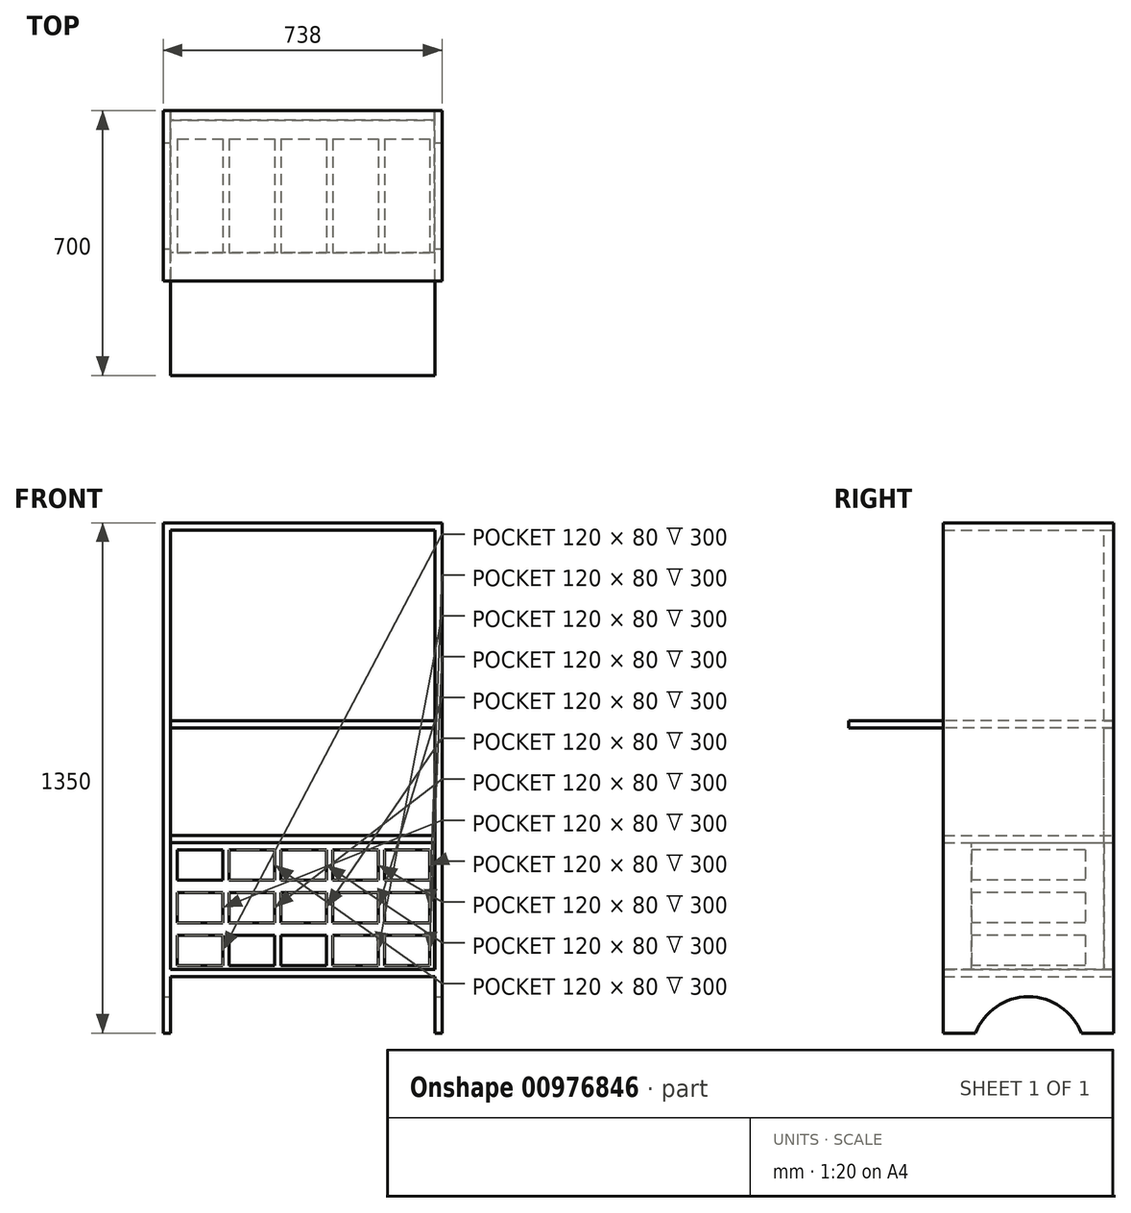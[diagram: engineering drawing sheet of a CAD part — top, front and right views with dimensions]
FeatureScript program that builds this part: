
annotation { "Feature Type Name" : "Feature", "Feature Type Description" : "" }
export const myFeature = defineFeature(function(context is Context, id is Id, definition is map)
    precondition{}
    {
        {
            var Q0;
            Q0=qCreatedBy(makeId("Front.planeOp"),FACE);
            var sketch = newSketch(context, id + "F0", { "sketchPlane" : qUnion([Q0])});
            skLineSegment(sketch, "E0.bottom", {"start": v(-369, 0) * mm, "end": v(-350, 0) * mm});
            skLineSegment(sketch, "E0.top", {"start": v(-369, 1350) * mm, "end": v(-350, 1350) * mm});
            skLineSegment(sketch, "E0.left", {"start": v(-369, 0) * mm, "end": v(-369, 1350) * mm});
            skLineSegment(sketch, "E0.right", {"start": v(-350, 0) * mm, "end": v(-350, 1350) * mm});
            skLineSegment(sketch, "E1", {"start": v(0, 1331) * mm, "end": v(0, 0) * mm, "construction": true});
            skLineSegment(sketch, "E2.MirrorCS", {"start": v(350, 0) * mm, "end": v(350, 1350) * mm});
            skLineSegment(sketch, "E3.MirrorCS", {"start": v(369, 0) * mm, "end": v(350, 0) * mm});
            skLineSegment(sketch, "E4.MirrorCS", {"start": v(369, 0) * mm, "end": v(369, 1350) * mm});
            skLineSegment(sketch, "E5.MirrorCS", {"start": v(369, 1350) * mm, "end": v(350, 1350) * mm});
            skLineSegment(sketch, "E6.bottom", {"start": v(-350, 1350) * mm, "end": v(350, 1350) * mm});
            skLineSegment(sketch, "E6.top", {"start": v(-350, 1331) * mm, "end": v(350, 1331) * mm});
            skLineSegment(sketch, "E6.left", {"start": v(-350, 1350) * mm, "end": v(-350, 1331) * mm});
            skLineSegment(sketch, "E6.right", {"start": v(350, 1350) * mm, "end": v(350, 1331) * mm});
            skSolve(sketch);
        }
        {
            var Q0;
            Q0=qSketchRegion(id+"F0",true);
            extrude(context, id + "F1", {"entities" : qUnion([Q0]), "depth" : 450 * mm});
        }
        {
            var Q0;
            Q0=makeQuery(id+"F1.opExtrude","SWEPT_FACE",FACE,{"disambiguationData":[OSD([sQuery(id+"F0.wireOp",EDGE,"E0.right")])]});
            var sketch = newSketch(context, id + "F2", { "sketchPlane" : qUnion([Q0])});
            skLineSegment(sketch, "E7.bottom", {"start": v(-450, 826.75) * mm, "end": v(0, 826.75) * mm});
            skLineSegment(sketch, "E7.top", {"start": v(-450, 807.75) * mm, "end": v(0, 807.75) * mm});
            skLineSegment(sketch, "E7.left", {"start": v(-450, 826.75) * mm, "end": v(-450, 807.75) * mm});
            skLineSegment(sketch, "E7.right", {"start": v(0, 826.75) * mm, "end": v(0, 807.75) * mm});
            skLineSegment(sketch, "E8.bottom", {"start": v(-450, 169) * mm, "end": v(0, 169) * mm});
            skLineSegment(sketch, "E8.top", {"start": v(-450, 150) * mm, "end": v(0, 150) * mm});
            skLineSegment(sketch, "E8.left", {"start": v(-450, 169) * mm, "end": v(-450, 150) * mm});
            skLineSegment(sketch, "E8.right", {"start": v(0, 169) * mm, "end": v(0, 150) * mm});
            skSolve(sketch);
        }
        {
            var Q0;
            Q0=makeQuery(id+"F2.imprint","IMPRINT",FACE,{"disambiguationData":[TD([[makeQuery(id+"F2.imprint","IMPRINT",EDGE,{"derivedFrom":sQuery(id+"F2.wireOp",EDGE,"E7.bottom")}),-1.0]])]});
            var Q1;
            Q1=makeQuery(id+"F2.imprint","IMPRINT",FACE,{"disambiguationData":[TD([[makeQuery(id+"F2.imprint","IMPRINT",EDGE,{"derivedFrom":sQuery(id+"F2.wireOp",EDGE,"E8.bottom")}),-1.0]])]});
            var Q2;
            Q2=qCreatedBy(makeId("Right.planeOp"),FACE);
            extrude(context, id + "F3", {"entities" : qUnion([Q0, Q1]), "operationType" : NewBodyOperationType.ADD, "endBound" : BoundingType.UP_TO_NEXT, "endBoundEntityFace" : qUnion([Q2]), "depth" : 25 * mm});
        }
        {
            var Q0;
            Q0=makeQuery(id+"F3.boolean.opBoolean","MERGE",FACE,{"derivedFrom":[makeQuery(id+"F1.opExtrude","CAP_FACE",FACE,{"disambiguationData":[OSD([sQuery(id+"F0.wireOp",EDGE,"E0.bottom"),sQuery(id+"F0.wireOp",EDGE,"E0.top"),sQuery(id+"F0.wireOp",EDGE,"E0.left"),sQuery(id+"F0.wireOp",EDGE,"E0.right"),sQuery(id+"F0.wireOp",EDGE,"KUvRnLVw-DjVN-ga7X-LMZa-ZJt3v3Kkx2uW.bottom"),sQuery(id+"F0.wireOp",EDGE,"KUvRnLVw-DjVN-ga7X-LMZa-ZJt3v3Kkx2uW.top"),sQuery(id+"F0.wireOp",EDGE,"KUvRnLVw-DjVN-ga7X-LMZa-ZJt3v3Kkx2uW.right")])],"isStart":true}),makeQuery(id+"F3.opExtrude","SWEPT_FACE",FACE,{"disambiguationData":[OSD([sQuery(id+"F2.wireOp",EDGE,"E7.right")])]})]});
            var sketch = newSketch(context, id + "F4", { "sketchPlane" : qUnion([Q0])});
            skLineSegment(sketch, "E9.bottom", {"start": v(350, 504.2) * mm, "end": v(-348.68, 504.2) * mm});
            skLineSegment(sketch, "E9.top", {"start": v(350, 154.2) * mm, "end": v(-348.68, 154.2) * mm});
            skLineSegment(sketch, "E9.left", {"start": v(350, 504.2) * mm, "end": v(350, 154.2) * mm});
            skLineSegment(sketch, "E9.right", {"start": v(-348.68, 504.2) * mm, "end": v(-348.68, 154.2) * mm});
            skSolve(sketch);
        }
        {
            var Q0;
            Q0=makeQuery(id+"F4.imprint","IMPRINT",FACE,{"disambiguationData":[TD([[makeQuery(id+"F4.imprint","IMPRINT",EDGE,{"derivedFrom":sQuery(id+"F4.wireOp",EDGE,"E9.bottom")}),1.0]])]});
            extrude(context, id + "F5", {"entities" : qUnion([Q0]), "operationType" : NewBodyOperationType.ADD, "oppositeDirection" : true, "depth" : 375 * mm});
        }
        {
            var Q0;
            Q0=makeQuery(id+"F5.opExtrude","CAP_FACE",FACE,{"disambiguationData":[OSD([sQuery(id+"F4.wireOp",EDGE,"E9.bottom"),sQuery(id+"F4.wireOp",EDGE,"E9.top"),sQuery(id+"F4.wireOp",EDGE,"E9.left"),sQuery(id+"F4.wireOp",EDGE,"E9.right")])],"isStart":false});
            var sketch = newSketch(context, id + "F6", { "sketchPlane" : qUnion([Q0])});
            skLineSegment(sketch, "E10.bottom", {"start": v(-331, 485.2) * mm, "end": v(-211, 485.2) * mm});
            skLineSegment(sketch, "E10.top", {"start": v(-331, 405.2) * mm, "end": v(-211, 405.2) * mm});
            skLineSegment(sketch, "E10.left", {"start": v(-331, 485.2) * mm, "end": v(-331, 405.2) * mm});
            skLineSegment(sketch, "E10.right", {"start": v(-211, 485.2) * mm, "end": v(-211, 405.2) * mm});
            skLineSegment(sketch, "E11.0.1.0", {"start": v(-331, 372) * mm, "end": v(-211, 372) * mm});
            skLineSegment(sketch, "E11.0.1.1", {"start": v(-211, 372) * mm, "end": v(-211, 292) * mm});
            skLineSegment(sketch, "E11.0.1.2", {"start": v(-331, 292) * mm, "end": v(-211, 292) * mm});
            skLineSegment(sketch, "E11.0.1.3", {"start": v(-331, 372) * mm, "end": v(-331, 292) * mm});
            skLineSegment(sketch, "E11.0.2.0", {"start": v(-331, 258.8) * mm, "end": v(-211, 258.8) * mm});
            skLineSegment(sketch, "E11.0.2.1", {"start": v(-211, 258.8) * mm, "end": v(-211, 178.8) * mm});
            skLineSegment(sketch, "E11.0.2.2", {"start": v(-331, 178.8) * mm, "end": v(-211, 178.8) * mm});
            skLineSegment(sketch, "E11.0.2.3", {"start": v(-331, 258.8) * mm, "end": v(-331, 178.8) * mm});
            skLineSegment(sketch, "E11.1.0.0", {"start": v(-194, 485.02) * mm, "end": v(-74, 485.02) * mm});
            skLineSegment(sketch, "E11.1.0.1", {"start": v(-74, 485.02) * mm, "end": v(-74, 405.02) * mm});
            skLineSegment(sketch, "E11.1.0.2", {"start": v(-194, 405.02) * mm, "end": v(-74, 405.02) * mm});
            skLineSegment(sketch, "E11.1.0.3", {"start": v(-194, 485.02) * mm, "end": v(-194, 405.02) * mm});
            skLineSegment(sketch, "E11.1.1.0", {"start": v(-194, 371.82) * mm, "end": v(-74, 371.82) * mm});
            skLineSegment(sketch, "E11.1.1.1", {"start": v(-74, 371.82) * mm, "end": v(-74, 291.82) * mm});
            skLineSegment(sketch, "E11.1.1.2", {"start": v(-194, 291.82) * mm, "end": v(-74, 291.82) * mm});
            skLineSegment(sketch, "E11.1.1.3", {"start": v(-194, 371.82) * mm, "end": v(-194, 291.82) * mm});
            skLineSegment(sketch, "E11.1.2.0", {"start": v(-194, 258.62) * mm, "end": v(-74, 258.62) * mm});
            skLineSegment(sketch, "E11.1.2.1", {"start": v(-74, 258.62) * mm, "end": v(-74, 178.62) * mm});
            skLineSegment(sketch, "E11.1.2.2", {"start": v(-194, 178.62) * mm, "end": v(-74, 178.62) * mm});
            skLineSegment(sketch, "E11.1.2.3", {"start": v(-194, 258.62) * mm, "end": v(-194, 178.62) * mm});
            skLineSegment(sketch, "E11.2.0.0", {"start": v(-57, 484.83) * mm, "end": v(63, 484.83) * mm});
            skLineSegment(sketch, "E11.2.0.1", {"start": v(63, 484.83) * mm, "end": v(63, 404.83) * mm});
            skLineSegment(sketch, "E11.2.0.2", {"start": v(-57, 404.83) * mm, "end": v(63, 404.83) * mm});
            skLineSegment(sketch, "E11.2.0.3", {"start": v(-57, 484.83) * mm, "end": v(-57, 404.83) * mm});
            skLineSegment(sketch, "E11.2.1.0", {"start": v(-57, 371.64) * mm, "end": v(63, 371.64) * mm});
            skLineSegment(sketch, "E11.2.1.1", {"start": v(63, 371.64) * mm, "end": v(63, 291.64) * mm});
            skLineSegment(sketch, "E11.2.1.2", {"start": v(-57, 291.64) * mm, "end": v(63, 291.64) * mm});
            skLineSegment(sketch, "E11.2.1.3", {"start": v(-57, 371.64) * mm, "end": v(-57, 291.64) * mm});
            skLineSegment(sketch, "E11.2.2.0", {"start": v(-57, 258.44) * mm, "end": v(63, 258.44) * mm});
            skLineSegment(sketch, "E11.2.2.1", {"start": v(63, 258.44) * mm, "end": v(63, 178.44) * mm});
            skLineSegment(sketch, "E11.2.2.2", {"start": v(-57, 178.44) * mm, "end": v(63, 178.44) * mm});
            skLineSegment(sketch, "E11.2.2.3", {"start": v(-57, 258.44) * mm, "end": v(-57, 178.44) * mm});
            skLineSegment(sketch, "E11.3.0.0", {"start": v(80, 484.65) * mm, "end": v(200, 484.65) * mm});
            skLineSegment(sketch, "E11.3.0.1", {"start": v(200, 484.65) * mm, "end": v(200, 404.65) * mm});
            skLineSegment(sketch, "E11.3.0.2", {"start": v(80, 404.65) * mm, "end": v(200, 404.65) * mm});
            skLineSegment(sketch, "E11.3.0.3", {"start": v(80, 484.65) * mm, "end": v(80, 404.65) * mm});
            skLineSegment(sketch, "E11.3.1.0", {"start": v(80, 371.45) * mm, "end": v(200, 371.45) * mm});
            skLineSegment(sketch, "E11.3.1.1", {"start": v(200, 371.45) * mm, "end": v(200, 291.45) * mm});
            skLineSegment(sketch, "E11.3.1.2", {"start": v(80, 291.45) * mm, "end": v(200, 291.45) * mm});
            skLineSegment(sketch, "E11.3.1.3", {"start": v(80, 371.45) * mm, "end": v(80, 291.45) * mm});
            skLineSegment(sketch, "E11.3.2.0", {"start": v(80, 258.26) * mm, "end": v(200, 258.26) * mm});
            skLineSegment(sketch, "E11.3.2.1", {"start": v(200, 258.26) * mm, "end": v(200, 178.26) * mm});
            skLineSegment(sketch, "E11.3.2.2", {"start": v(80, 178.26) * mm, "end": v(200, 178.26) * mm});
            skLineSegment(sketch, "E11.3.2.3", {"start": v(80, 258.26) * mm, "end": v(80, 178.26) * mm});
            skLineSegment(sketch, "E11.4.0.0", {"start": v(217, 484.47) * mm, "end": v(337, 484.47) * mm});
            skLineSegment(sketch, "E11.4.0.1", {"start": v(337, 484.47) * mm, "end": v(337, 404.47) * mm});
            skLineSegment(sketch, "E11.4.0.2", {"start": v(217, 404.47) * mm, "end": v(337, 404.47) * mm});
            skLineSegment(sketch, "E11.4.0.3", {"start": v(217, 484.47) * mm, "end": v(217, 404.47) * mm});
            skLineSegment(sketch, "E11.4.1.0", {"start": v(217, 371.27) * mm, "end": v(337, 371.27) * mm});
            skLineSegment(sketch, "E11.4.1.1", {"start": v(337, 371.27) * mm, "end": v(337, 291.27) * mm});
            skLineSegment(sketch, "E11.4.1.2", {"start": v(217, 291.27) * mm, "end": v(337, 291.27) * mm});
            skLineSegment(sketch, "E11.4.1.3", {"start": v(217, 371.27) * mm, "end": v(217, 291.27) * mm});
            skLineSegment(sketch, "E11.4.2.0", {"start": v(217, 258.07) * mm, "end": v(337, 258.07) * mm});
            skLineSegment(sketch, "E11.4.2.1", {"start": v(337, 258.07) * mm, "end": v(337, 178.07) * mm});
            skLineSegment(sketch, "E11.4.2.2", {"start": v(217, 178.07) * mm, "end": v(337, 178.07) * mm});
            skLineSegment(sketch, "E11.4.2.3", {"start": v(217, 258.07) * mm, "end": v(217, 178.07) * mm});
            skLineSegment(sketch, "E11.direction1", {"start": v(-331, 485.2) * mm, "end": v(-194, 485.02) * mm, "construction": true});
            skLineSegment(sketch, "E11.direction2", {"start": v(-331, 485.2) * mm, "end": v(-331, 372) * mm, "construction": true});
            skSolve(sketch);
        }
        {
            var Q0;
            Q0=makeQuery(id+"F6.imprint","IMPRINT",FACE,{"disambiguationData":[TD([[makeQuery(id+"F6.imprint","IMPRINT",EDGE,{"derivedFrom":sQuery(id+"F6.wireOp",EDGE,"E10.bottom")}),-1.0]])]});
            var Q1;
            Q1=makeQuery(id+"F6.imprint","IMPRINT",FACE,{"disambiguationData":[TD([[makeQuery(id+"F6.imprint","IMPRINT",EDGE,{"derivedFrom":sQuery(id+"F6.wireOp",EDGE,"E11.1.0.0")}),-1.0]])]});
            var Q2;
            Q2=makeQuery(id+"F6.imprint","IMPRINT",FACE,{"disambiguationData":[TD([[makeQuery(id+"F6.imprint","IMPRINT",EDGE,{"derivedFrom":sQuery(id+"F6.wireOp",EDGE,"E11.2.0.0")}),-1.0]])]});
            var Q3;
            Q3=makeQuery(id+"F6.imprint","IMPRINT",FACE,{"disambiguationData":[TD([[makeQuery(id+"F6.imprint","IMPRINT",EDGE,{"derivedFrom":sQuery(id+"F6.wireOp",EDGE,"E11.3.0.0")}),-1.0]])]});
            var Q4;
            Q4=makeQuery(id+"F6.imprint","IMPRINT",FACE,{"disambiguationData":[TD([[makeQuery(id+"F6.imprint","IMPRINT",EDGE,{"derivedFrom":sQuery(id+"F6.wireOp",EDGE,"E11.4.0.0")}),-1.0]])]});
            var Q5;
            Q5=makeQuery(id+"F6.imprint","IMPRINT",FACE,{"disambiguationData":[TD([[makeQuery(id+"F6.imprint","IMPRINT",EDGE,{"derivedFrom":sQuery(id+"F6.wireOp",EDGE,"E11.0.1.0")}),-1.0]])]});
            var Q6;
            Q6=makeQuery(id+"F6.imprint","IMPRINT",FACE,{"disambiguationData":[TD([[makeQuery(id+"F6.imprint","IMPRINT",EDGE,{"derivedFrom":sQuery(id+"F6.wireOp",EDGE,"E11.1.1.0")}),-1.0]])]});
            var Q7;
            Q7=makeQuery(id+"F6.imprint","IMPRINT",FACE,{"disambiguationData":[TD([[makeQuery(id+"F6.imprint","IMPRINT",EDGE,{"derivedFrom":sQuery(id+"F6.wireOp",EDGE,"E11.2.1.0")}),-1.0]])]});
            var Q8;
            Q8=makeQuery(id+"F6.imprint","IMPRINT",FACE,{"disambiguationData":[TD([[makeQuery(id+"F6.imprint","IMPRINT",EDGE,{"derivedFrom":sQuery(id+"F6.wireOp",EDGE,"E11.3.1.0")}),-1.0]])]});
            var Q9;
            Q9=makeQuery(id+"F6.imprint","IMPRINT",FACE,{"disambiguationData":[TD([[makeQuery(id+"F6.imprint","IMPRINT",EDGE,{"derivedFrom":sQuery(id+"F6.wireOp",EDGE,"E11.4.1.0")}),-1.0]])]});
            var Q10;
            Q10=makeQuery(id+"F6.imprint","IMPRINT",FACE,{"disambiguationData":[TD([[makeQuery(id+"F6.imprint","IMPRINT",EDGE,{"derivedFrom":sQuery(id+"F6.wireOp",EDGE,"E11.0.2.0")}),-1.0]])]});
            var Q11;
            Q11=makeQuery(id+"F6.imprint","IMPRINT",FACE,{"disambiguationData":[TD([[makeQuery(id+"F6.imprint","IMPRINT",EDGE,{"derivedFrom":sQuery(id+"F6.wireOp",EDGE,"E11.1.2.0")}),-1.0]])]});
            var Q12;
            Q12=makeQuery(id+"F6.imprint","IMPRINT",FACE,{"disambiguationData":[TD([[makeQuery(id+"F6.imprint","IMPRINT",EDGE,{"derivedFrom":sQuery(id+"F6.wireOp",EDGE,"E11.2.2.0")}),-1.0]])]});
            var Q13;
            Q13=makeQuery(id+"F6.imprint","IMPRINT",FACE,{"disambiguationData":[TD([[makeQuery(id+"F6.imprint","IMPRINT",EDGE,{"derivedFrom":sQuery(id+"F6.wireOp",EDGE,"E11.3.2.0")}),-1.0]])]});
            var Q14;
            Q14=makeQuery(id+"F6.imprint","IMPRINT",FACE,{"disambiguationData":[TD([[makeQuery(id+"F6.imprint","IMPRINT",EDGE,{"derivedFrom":sQuery(id+"F6.wireOp",EDGE,"E11.4.2.0")}),-1.0]])]});
            extrude(context, id + "F7", {"entities" : qUnion([Q0, Q1, Q2, Q3, Q4, Q5, Q6, Q7, Q8, Q9, Q10, Q11, Q12, Q13, Q14]), "operationType" : NewBodyOperationType.REMOVE, "oppositeDirection" : true, "depth" : 300 * mm});
        }
        {
            var Q0;
            Q0=makeQuery(id+"F1.opExtrude","SWEPT_FACE",FACE,{"disambiguationData":[OSD([sQuery(id+"F0.wireOp",EDGE,"E4.MirrorCS")])]});
            var sketch = newSketch(context, id + "F8", { "sketchPlane" : qUnion([Q0])});
            skArc(sketch, "E12", {"start": v(-85, 0) * mm, "mid": v(-225, 96.15) * mm, "end": v(-365, 0) * mm});
            skLineSegment(sketch, "E13", {"start": v(-365, 0) * mm, "end": v(-85, 0) * mm});
            skSolve(sketch);
        }
        {
            var Q0;
            Q0=qSketchRegion(id+"F8",true);
            extrude(context, id + "F9", {"entities" : qUnion([Q0]), "operationType" : NewBodyOperationType.REMOVE, "endBound" : BoundingType.THROUGH_ALL, "oppositeDirection" : true, "depth" : 25 * mm});
        }
        {
            var Q0;
            {var subQ0=sQuery(id+"F2.wireOp",EDGE,"E8.right");var subQ1=sQuery(id+"F0.wireOp",EDGE,"E0.right");Q0=makeQuery(id+"F5.boolean.opBoolean","MERGE",FACE,{"derivedFrom":[makeQuery(id+"F3.boolean.opBoolean","MERGE",FACE,{"derivedFrom":[makeQuery(id+"F1.opExtrude","CAP_FACE",FACE,{"disambiguationData":[OSD([sQuery(id+"F0.wireOp",EDGE,"E0.bottom"),sQuery(id+"F0.wireOp",EDGE,"E0.top"),sQuery(id+"F0.wireOp",EDGE,"E0.left"),subQ1,sQuery(id+"F0.wireOp",EDGE,"E2.MirrorCS"),sQuery(id+"F0.wireOp",EDGE,"E3.MirrorCS"),sQuery(id+"F0.wireOp",EDGE,"E4.MirrorCS"),sQuery(id+"F0.wireOp",EDGE,"E5.MirrorCS"),sQuery(id+"F0.wireOp",EDGE,"E6.bottom"),sQuery(id+"F0.wireOp",EDGE,"E6.top")])],"isStart":true}),makeQuery(id+"F3.opExtrude","SWEPT_FACE",FACE,{"disambiguationData":[OSD([sQuery(id+"F2.wireOp",EDGE,"E7.right")])]}),makeQuery(id+"F3.opExtrude","SWEPT_FACE",FACE,{"disambiguationData":[OSD([subQ0])]})]}),makeQuery(id+"F5.opExtrude","CAP_FACE",FACE,{"disambiguationData":[OSD([subQ1,sQuery(id+"F2.wireOp",EDGE,"E8.bottom"),subQ0,sQuery(id+"F4.wireOp",EDGE,"E9.bottom"),sQuery(id+"F4.wireOp",EDGE,"E9.left"),sQuery(id+"F4.wireOp",EDGE,"E9.right")])],"isStart":true})]});}
            var sketch = newSketch(context, id + "F10", { "sketchPlane" : qUnion([Q0])});
            skLineSegment(sketch, "E14.bottom", {"start": v(-350, 1331) * mm, "end": v(350, 1331) * mm});
            skLineSegment(sketch, "E14.top", {"start": v(-350, 826.75) * mm, "end": v(350, 826.75) * mm});
            skLineSegment(sketch, "E14.left", {"start": v(-350, 1331) * mm, "end": v(-350, 826.75) * mm});
            skLineSegment(sketch, "E14.right", {"start": v(350, 1331) * mm, "end": v(350, 826.75) * mm});
            skSolve(sketch);
        }
        {
            var Q0;
            Q0=makeQuery(id+"F10.imprint","IMPRINT",FACE,{"disambiguationData":[TD([[makeQuery(id+"F10.imprint","IMPRINT",EDGE,{"derivedFrom":sQuery(id+"F10.wireOp",EDGE,"E14.bottom")}),1.0]])]});
            extrude(context, id + "F11", {"entities" : qUnion([Q0]), "oppositeDirection" : true, "depth" : 25 * mm});
        }
        {
            var Q0;
            {var subQ0=sQuery(id+"F2.wireOp",EDGE,"E8.right");var subQ1=sQuery(id+"F0.wireOp",EDGE,"E0.right");Q0=makeQuery(id+"F5.boolean.opBoolean","MERGE",FACE,{"derivedFrom":[makeQuery(id+"F3.boolean.opBoolean","MERGE",FACE,{"derivedFrom":[makeQuery(id+"F1.opExtrude","CAP_FACE",FACE,{"disambiguationData":[OSD([sQuery(id+"F0.wireOp",EDGE,"E0.bottom"),sQuery(id+"F0.wireOp",EDGE,"E0.top"),sQuery(id+"F0.wireOp",EDGE,"E0.left"),subQ1,sQuery(id+"F0.wireOp",EDGE,"E2.MirrorCS"),sQuery(id+"F0.wireOp",EDGE,"E3.MirrorCS"),sQuery(id+"F0.wireOp",EDGE,"E4.MirrorCS"),sQuery(id+"F0.wireOp",EDGE,"E5.MirrorCS"),sQuery(id+"F0.wireOp",EDGE,"E6.bottom"),sQuery(id+"F0.wireOp",EDGE,"E6.top")])],"isStart":true}),makeQuery(id+"F3.opExtrude","SWEPT_FACE",FACE,{"disambiguationData":[OSD([sQuery(id+"F2.wireOp",EDGE,"E7.right")])]}),makeQuery(id+"F3.opExtrude","SWEPT_FACE",FACE,{"disambiguationData":[OSD([subQ0])]})]}),makeQuery(id+"F5.opExtrude","CAP_FACE",FACE,{"disambiguationData":[OSD([subQ1,sQuery(id+"F2.wireOp",EDGE,"E8.bottom"),subQ0,sQuery(id+"F4.wireOp",EDGE,"E9.bottom"),sQuery(id+"F4.wireOp",EDGE,"E9.left"),sQuery(id+"F4.wireOp",EDGE,"E9.right")])],"isStart":true})]});}
            var sketch = newSketch(context, id + "F12", { "sketchPlane" : qUnion([Q0])});
            skSolve(sketch);
        }
        {
            var Q0;
            Q0=makeQuery(id+"F12.imprint","IMPRINT",FACE,{"disambiguationData":[TD([[makeQuery(id+"F12.imprint","IMPRINT",EDGE,{"derivedFrom":makeQuery(id+"F5.opExtrude","CAP_EDGE",EDGE,{"disambiguationData":[OSD([sQuery(id+"F4.wireOp",EDGE,"E9.bottom")])],"isStart":true})}),-1.0]])]});
            extrude(context, id + "F13", {"entities" : qUnion([Q0]), "oppositeDirection" : true, "depth" : 25 * mm});
        }
        {
            var Q0;
            {var subQ6=sQuery(id+"F0.wireOp",EDGE,"E0.right");Q0=makeQuery(id+"F3.boolean.opBoolean","SPLIT",FACE,{"disambiguationData":[TD([makeQuery(id+"F3.opExtrude","SWEPT_FACE",FACE,{"disambiguationData":[OSD([sQuery(id+"F2.wireOp",EDGE,"E7.top")])]})])],"derivedFrom":makeQuery(id+"F1.opExtrude","SWEPT_FACE",FACE,{"disambiguationData":[OSD([subQ6])]})});}
            var sketch = newSketch(context, id + "F14", { "sketchPlane" : qUnion([Q0])});
            skLineSegment(sketch, "E15.bottom", {"start": v(0, 523.2) * mm, "end": v(-450, 523.2) * mm});
            skLineSegment(sketch, "E15.top", {"start": v(0, 504.2) * mm, "end": v(-450, 504.2) * mm});
            skLineSegment(sketch, "E15.left", {"start": v(0, 523.2) * mm, "end": v(0, 504.2) * mm});
            skLineSegment(sketch, "E15.right", {"start": v(-450, 523.2) * mm, "end": v(-450, 504.2) * mm});
            skSolve(sketch);
        }
        {
            var Q0;
            Q0=makeQuery(id+"F14.imprint","IMPRINT",FACE,{"disambiguationData":[TD([[makeQuery(id+"F14.imprint","IMPRINT",EDGE,{"derivedFrom":sQuery(id+"F14.wireOp",EDGE,"E15.bottom")}),1.0]])]});
            extrude(context, id + "F15", {"entities" : qUnion([Q0]), "endBound" : BoundingType.UP_TO_NEXT, "depth" : 25 * mm});
        }
        {
            var Q0;
            Q0=makeQuery(id+"F3.boolean.opBoolean","MERGE",FACE,{"derivedFrom":[makeQuery(id+"F1.opExtrude","CAP_FACE",FACE,{"disambiguationData":[OSD([sQuery(id+"F0.wireOp",EDGE,"E0.bottom"),sQuery(id+"F0.wireOp",EDGE,"E0.top"),sQuery(id+"F0.wireOp",EDGE,"E0.left"),sQuery(id+"F0.wireOp",EDGE,"E0.right"),sQuery(id+"F0.wireOp",EDGE,"E2.MirrorCS"),sQuery(id+"F0.wireOp",EDGE,"E3.MirrorCS"),sQuery(id+"F0.wireOp",EDGE,"E4.MirrorCS"),sQuery(id+"F0.wireOp",EDGE,"E5.MirrorCS"),sQuery(id+"F0.wireOp",EDGE,"E6.bottom"),sQuery(id+"F0.wireOp",EDGE,"E6.top")])],"isStart":false}),makeQuery(id+"F3.opExtrude","SWEPT_FACE",FACE,{"disambiguationData":[OSD([sQuery(id+"F2.wireOp",EDGE,"E7.left")])]}),makeQuery(id+"F3.opExtrude","SWEPT_FACE",FACE,{"disambiguationData":[OSD([sQuery(id+"F2.wireOp",EDGE,"E8.left")])]})]});
            var sketch = newSketch(context, id + "F16", { "sketchPlane" : qUnion([Q0])});
            skLineSegment(sketch, "E16.bottom", {"start": v(-350, 826.75) * mm, "end": v(350, 826.75) * mm});
            skLineSegment(sketch, "E16.top", {"start": v(-350, 807.75) * mm, "end": v(350, 807.75) * mm});
            skLineSegment(sketch, "E16.left", {"start": v(-350, 826.75) * mm, "end": v(-350, 807.75) * mm});
            skLineSegment(sketch, "E16.right", {"start": v(350, 826.75) * mm, "end": v(350, 807.75) * mm});
            skSolve(sketch);
        }
        {
            var Q0;
            Q0=makeQuery(id+"F16.imprint","IMPRINT",FACE,{"disambiguationData":[TD([[makeQuery(id+"F16.imprint","IMPRINT",EDGE,{"derivedFrom":sQuery(id+"F16.wireOp",EDGE,"E16.bottom")}),1.0]])]});
            extrude(context, id + "F17", {"entities" : qUnion([Q0]), "operationType" : NewBodyOperationType.ADD, "depth" : 250 * mm});
        }
    });
